# Revit family: NBS_GreshamOfficeFurnitureLtd_OffcChrs_Klyro-MeetingChair
name_source: partatom
category: Furniture
units: mm (PartAtom-declared; Revit-internal decimal feet)

## family parameters
Always vertical = Yes
Cut with Voids When Loaded = No
Room Calculation Point = No
Shared = No
Work Plane-Based = No

## types (5) — shared parameters
AssetType = Fixed
Category = Pr_40_50_12_57:Office chairs
DurationUnit = year
HighestSeatingHeight = 490 mm
IfcExportAs = IfcFurnitureType
IfcExportType = CHAIR
IsBuiltIn = No
LowestSeatingHeight = 490 mm
ManufacturerName = Gresham Office Furniture Ltd
ManufacturerURL = www.gof.co.uk
NBSCertification = www.nationalbimlibrary.com/cert/1qsadg0t
NBSDescription = Office chairs
NBSReference = 45-35-20/330
NominalDepth = 630 mm
NominalHeight = 870 mm
NominalLength = 580 mm
Recyclability = 100%
SeatingHeight = 490 mm
SeatsAndBacksMaterial = Cold-cure moulded polyurethane foam
Size = 870 x 580 x 630 mm
StandardsDurability = To BS EN 16139:2013+AC2013 Level 2
Status = UNSET
Uniclass2015Code = Pr_40_50_12_57
Uniclass2015Title = Office chairs
Uniclass2015Version = Products v1.23
Version = 1
WarrantyDescription = Five year
WarrantyDurationUnit = year
zero-valued in all types: NominalWidth

## per-type parameters (varying)
| type | 4LegSwivelBase | BIMObjectName | BaseColour | BaseType | Material | ModelReference | Name | PyramidSwivelBase | SeatHeight | SledBase | Wooden4LegBase | WoodenSpindleBase |
| Wooden4LegBase_KLY1AR1 | No | NBS_GreshamOfficeFurnitureLtd_OfficeChairs_Klyro-MeetingChair_KLY1AR1 | Dark walnut; Natural | Four legged base | Polyurethane, Wood, Fabric | KLY1AR1 | OfficeChairs_Klyro-MeetingChair_KLY1AR1_GreshamOfficeFurnitureLtd | No | 366 mm | No | Yes | No |
| WoodenSpindleBase_KLY1AR8 | No | NBS_GreshamOfficeFurnitureLtd_OfficeChairs_Klyro-MeetingChair_KLY1AR8 | Dark walnut; Natural | Spindle base | Polyurethane, Wood, Fabric | KLY1AR8 | OfficeChairs_Klyro-MeetingChair_KLY1AR8_GreshamOfficeFurnitureLtd | No | 366 mm | No | No | Yes |
| SledBase_KLY1AR7 | No | NBS_GreshamOfficeFurnitureLtd_OfficeChairs_Klyro-MeetingChair_KLY1AR7 | Black; Grey; Silver; White; Chrome | Sled base | Polyurethane, Metal, Fabric | KLY1AR7 | OfficeChairs_Klyro-MeetingChair_KLY1AR7_GreshamOfficeFurnitureLtd | No | 391 mm | Yes | No | No |
| 4LegSwivelBase_KLY1AR5 | Yes | NBS_GreshamOfficeFurnitureLtd_OfficeChairs_Klyro-MeetingChair_KLY1AR5 | Black; Grey; Silver; White; Chrome | Four legged swivel base | Polyurethane, Metal, Fabric | KLY1AR5 | OfficeChairs_Klyro-MeetingChair_KLY1AR5_GreshamOfficeFurnitureLtd | No | 366 mm | No | No | No |
| PyramidSwivelBase_KLY1AR6 | No | NBS_GreshamOfficeFurnitureLtd_OfficeChairs_Klyro-MeetingChair_KLY1AR6 | Black; Grey; Silver; White; Chrome | Pyramid swivel base | Polyurethane, Metal, Fabric | KLY1AR6 | OfficeChairs_Klyro-MeetingChair_KLY1AR6_GreshamOfficeFurnitureLtd | Yes | 384 mm  [stored 1.25984 ft] | No | No | No |

note: [stored X ft] marks values corroborated as IEEE doubles in the binary element streams (Revit-internal decimal feet)

## geometry (parser evidence)
native form markers: Sweep x24
no freeform markers — native parametric forms only
